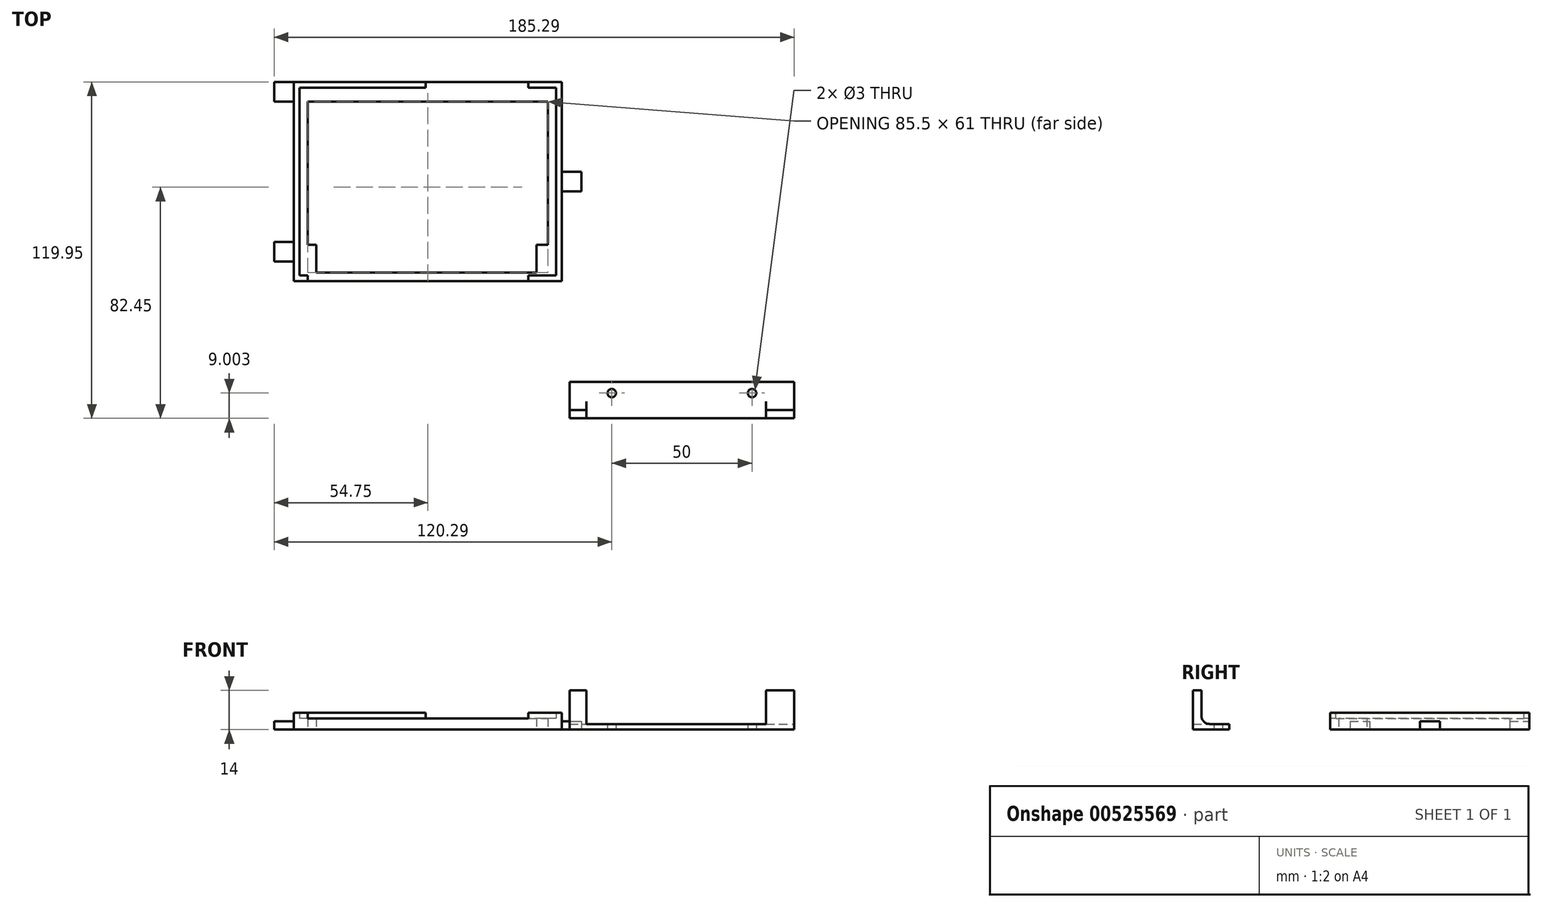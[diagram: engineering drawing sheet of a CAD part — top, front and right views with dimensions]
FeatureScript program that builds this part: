
annotation { "Feature Type Name" : "Feature", "Feature Type Description" : "" }
export const myFeature = defineFeature(function(context is Context, id is Id, definition is map)
    precondition{}
    {
        {
            var Q0;
            Q0=qCreatedBy(makeId("Top.planeOp"),FACE);
            var sketch = newSketch(context, id + "F0", { "sketchPlane" : qUnion([Q0])});
            skLineSegment(sketch, "E0.bottom", {"start": v(45.75, -33.5) * mm, "end": v(-45.75, -33.5) * mm});
            skLineSegment(sketch, "E0.top", {"start": v(45.75, 33.5) * mm, "end": v(-45.75, 33.5) * mm});
            skLineSegment(sketch, "E0.left", {"start": v(45.75, -33.5) * mm, "end": v(45.75, 33.5) * mm});
            skLineSegment(sketch, "E0.right", {"start": v(-45.75, -33.5) * mm, "end": v(-45.75, 33.5) * mm});
            skPoint(sketch, "E0.middle", {"position": v(0, 0) * mm});
            skLineSegment(sketch, "E1.bottom", {"start": v(47.75, -35.5) * mm, "end": v(-47.75, -35.5) * mm});
            skLineSegment(sketch, "E1.top", {"start": v(47.75, 35.5) * mm, "end": v(-47.75, 35.5) * mm});
            skLineSegment(sketch, "E1.left", {"start": v(47.75, -35.5) * mm, "end": v(47.75, 35.5) * mm});
            skLineSegment(sketch, "E1.right", {"start": v(-47.75, -35.5) * mm, "end": v(-47.75, 35.5) * mm});
            skSolve(sketch);
        }
        {
            var Q0;
            Q0=qSketchRegion(id+"F0",true);
            extrude(context, id + "F1", {"entities" : qUnion([Q0]), "depth" : 6 * mm, "offsetDistance" : 25 * mm});
        }
        {
            var Q0;
            Q0=makeQuery(id+"F1.opExtrude","CAP_FACE",FACE,{"disambiguationData":[OSD([sQuery(id+"F0.wireOp",EDGE,"E0.bottom"),sQuery(id+"F0.wireOp",EDGE,"E0.top"),sQuery(id+"F0.wireOp",EDGE,"E0.left"),sQuery(id+"F0.wireOp",EDGE,"E0.right"),sQuery(id+"F0.wireOp",EDGE,"E1.bottom"),sQuery(id+"F0.wireOp",EDGE,"E1.top"),sQuery(id+"F0.wireOp",EDGE,"E1.left"),sQuery(id+"F0.wireOp",EDGE,"E1.right")])],"isStart":true});
            var sketch = newSketch(context, id + "F2", { "sketchPlane" : qUnion([Q0])});
            skLineSegment(sketch, "E2.bottom", {"start": v(45.75, 33.5) * mm, "end": v(-45.75, 33.5) * mm});
            skLineSegment(sketch, "E2.top", {"start": v(45.75, -33.5) * mm, "end": v(-45.75, -33.5) * mm});
            skLineSegment(sketch, "E2.left", {"start": v(45.75, 33.5) * mm, "end": v(45.75, -33.5) * mm});
            skLineSegment(sketch, "E2.right", {"start": v(-45.75, 33.5) * mm, "end": v(-45.75, -33.5) * mm});
            skPoint(sketch, "E2.middle", {"position": v(0, 0) * mm});
            skLineSegment(sketch, "E3.bottom", {"start": v(-42.75, -28.5) * mm, "end": v(-30.75, -28.5) * mm});
            skLineSegment(sketch, "E3.top", {"start": v(-39.75, 32.5) * mm, "end": v(38.75, 32.5) * mm});
            skLineSegment(sketch, "E3.left", {"start": v(-42.75, -28.5) * mm, "end": v(-42.75, 22.5) * mm});
            skLineSegment(sketch, "E3.right", {"start": v(42.75, -28.5) * mm, "end": v(42.75, 22.5) * mm});
            skLineSegment(sketch, "E4", {"start": v(42.75, 22.5) * mm, "end": v(38.75, 22.5) * mm});
            skLineSegment(sketch, "E5", {"start": v(38.75, 22.5) * mm, "end": v(38.75, 32.5) * mm});
            skLineSegment(sketch, "E6", {"start": v(-30.75, -28.5) * mm, "end": v(-30.75, -28.5) * mm});
            skLineSegment(sketch, "E7", {"start": v(-30.75, -28.5) * mm, "end": v(-20.75, -28.5) * mm});
            skLineSegment(sketch, "E8", {"start": v(-20.75, -28.5) * mm, "end": v(-20.75, -28.5) * mm});
            skLineSegment(sketch, "E9.trimOffspring", {"start": v(-20.75, -28.5) * mm, "end": v(42.75, -28.5) * mm});
            skLineSegment(sketch, "E10", {"start": v(-42.75, 22.5) * mm, "end": v(-39.75, 22.5) * mm});
            skLineSegment(sketch, "E11", {"start": v(-39.75, 22.5) * mm, "end": v(-39.75, 32.5) * mm});
            skSolve(sketch);
        }
        {
            var Q0;
            Q0=qSketchRegion(id+"F2",true);
            extrude(context, id + "F3", {"entities" : qUnion([Q0]), "operationType" : NewBodyOperationType.ADD, "oppositeDirection" : true, "depth" : 4 * mm, "offsetDistance" : 25 * mm});
        }
        {
            var Q0;
            Q0=makeQuery(id+"F1.opExtrude","CAP_FACE",FACE,{"disambiguationData":[OSD([sQuery(id+"F0.wireOp",EDGE,"E0.bottom"),sQuery(id+"F0.wireOp",EDGE,"E0.top"),sQuery(id+"F0.wireOp",EDGE,"E0.left"),sQuery(id+"F0.wireOp",EDGE,"E0.right"),sQuery(id+"F0.wireOp",EDGE,"E1.bottom"),sQuery(id+"F0.wireOp",EDGE,"E1.top"),sQuery(id+"F0.wireOp",EDGE,"E1.left"),sQuery(id+"F0.wireOp",EDGE,"E1.right")])],"isStart":false});
            var sketch = newSketch(context, id + "F4", { "sketchPlane" : qUnion([Q0])});
            skLineSegment(sketch, "E12.bottom", {"start": v(-42.75, -33.5) * mm, "end": v(35.75, -33.5) * mm});
            skLineSegment(sketch, "E12.top", {"start": v(-42.75, -35.5) * mm, "end": v(35.75, -35.5) * mm});
            skLineSegment(sketch, "E12.left", {"start": v(-42.75, -33.5) * mm, "end": v(-42.75, -35.5) * mm});
            skLineSegment(sketch, "E12.right", {"start": v(35.75, -33.5) * mm, "end": v(35.75, -35.5) * mm});
            skLineSegment(sketch, "E13.bottom", {"start": v(-0.75, 35.5) * mm, "end": v(35.75, 35.5) * mm});
            skLineSegment(sketch, "E13.top", {"start": v(-0.75, 33.5) * mm, "end": v(35.75, 33.5) * mm});
            skLineSegment(sketch, "E13.left", {"start": v(-0.75, 35.5) * mm, "end": v(-0.75, 33.5) * mm});
            skLineSegment(sketch, "E13.right", {"start": v(35.75, 35.5) * mm, "end": v(35.75, 33.5) * mm});
            skSolve(sketch);
        }
        {
            var Q0;
            Q0=qSketchRegion(id+"F4",true);
            extrude(context, id + "F5", {"entities" : qUnion([Q0]), "operationType" : NewBodyOperationType.REMOVE, "oppositeDirection" : true, "depth" : 2 * mm, "offsetDistance" : 25 * mm});
        }
        {
            var Q0;
            Q0=makeQuery(id+"F3.boolean.opBoolean","MERGE",FACE,{"derivedFrom":[makeQuery(id+"F1.opExtrude","CAP_FACE",FACE,{"disambiguationData":[OSD([sQuery(id+"F0.wireOp",EDGE,"E0.bottom"),sQuery(id+"F0.wireOp",EDGE,"E0.top"),sQuery(id+"F0.wireOp",EDGE,"E0.left"),sQuery(id+"F0.wireOp",EDGE,"E0.right"),sQuery(id+"F0.wireOp",EDGE,"E1.bottom"),sQuery(id+"F0.wireOp",EDGE,"E1.top"),sQuery(id+"F0.wireOp",EDGE,"E1.left"),sQuery(id+"F0.wireOp",EDGE,"E1.right")])],"isStart":true}),makeQuery(id+"F3.opExtrude","CAP_FACE",FACE,{"disambiguationData":[OSD([sQuery(id+"F2.wireOp",EDGE,"E2.bottom"),sQuery(id+"F2.wireOp",EDGE,"E2.top"),sQuery(id+"F2.wireOp",EDGE,"E2.left"),sQuery(id+"F2.wireOp",EDGE,"E2.right"),sQuery(id+"F2.wireOp",EDGE,"E3.bottom"),sQuery(id+"F2.wireOp",EDGE,"E3.top"),sQuery(id+"F2.wireOp",EDGE,"E3.left"),sQuery(id+"F2.wireOp",EDGE,"E3.right"),sQuery(id+"F2.wireOp",EDGE,"E4"),sQuery(id+"F2.wireOp",EDGE,"E5"),sQuery(id+"F2.wireOp",EDGE,"E6"),sQuery(id+"F2.wireOp",EDGE,"E7"),sQuery(id+"F2.wireOp",EDGE,"E8"),sQuery(id+"F2.wireOp",EDGE,"E9.trimOffspring")])],"isStart":true})]});
            var sketch = newSketch(context, id + "F6", { "sketchPlane" : qUnion([Q0])});
            skLineSegment(sketch, "E14.bottom", {"start": v(-47.75, 21.5) * mm, "end": v(-54.75, 21.5) * mm});
            skLineSegment(sketch, "E14.top", {"start": v(-47.75, 28.5) * mm, "end": v(-54.75, 28.5) * mm});
            skLineSegment(sketch, "E14.left", {"start": v(-47.75, 21.5) * mm, "end": v(-47.75, 28.5) * mm});
            skLineSegment(sketch, "E14.right", {"start": v(-54.75, 21.5) * mm, "end": v(-54.75, 28.5) * mm});
            skLineSegment(sketch, "E15.bottom", {"start": v(-47.75, -35.5) * mm, "end": v(-54.75, -35.5) * mm});
            skLineSegment(sketch, "E15.top", {"start": v(-47.75, -28.5) * mm, "end": v(-54.75, -28.5) * mm});
            skLineSegment(sketch, "E15.left", {"start": v(-47.75, -35.5) * mm, "end": v(-47.75, -28.5) * mm});
            skLineSegment(sketch, "E15.right", {"start": v(-54.75, -35.5) * mm, "end": v(-54.75, -28.5) * mm});
            skPoint(sketch, "E16", {"position": v(-51.25, -32) * mm});
            skPoint(sketch, "E16.positionSnap0", {"position": v(-51.25, -35.5) * mm});
            skPoint(sketch, "E16.positionSnap1", {"position": v(-54.75, -32) * mm});
            skPoint(sketch, "E17", {"position": v(-51.25, 25) * mm});
            skPoint(sketch, "E17.positionSnap0", {"position": v(-51.25, 21.5) * mm});
            skPoint(sketch, "E17.positionSnap1", {"position": v(-54.75, 25) * mm});
            skLineSegment(sketch, "E18.bottom", {"start": v(47.75, -3.5) * mm, "end": v(54.75, -3.5) * mm});
            skLineSegment(sketch, "E18.top", {"start": v(47.75, 3.5) * mm, "end": v(54.75, 3.5) * mm});
            skLineSegment(sketch, "E18.left", {"start": v(47.75, -3.5) * mm, "end": v(47.75, 3.5) * mm});
            skLineSegment(sketch, "E18.right", {"start": v(54.75, -3.5) * mm, "end": v(54.75, 3.5) * mm});
            skPoint(sketch, "E19", {"position": v(51.25, 0) * mm});
            skPoint(sketch, "E19.positionSnap0", {"position": v(54.75, 0) * mm});
            skPoint(sketch, "E19.positionSnap1", {"position": v(51.25, 3.5) * mm});
            skSolve(sketch);
        }
        {
            var Q0;
            Q0=qSketchRegion(id+"F6",true);
            extrude(context, id + "F7", {"entities" : qUnion([Q0]), "operationType" : NewBodyOperationType.ADD, "oppositeDirection" : true, "depth" : 3 * mm, "offsetDistance" : 25 * mm});
        }
        {
            var Q0;
            Q0=qCreatedBy(makeId("Top.planeOp"),FACE);
            var sketch = newSketch(context, id + "F8", { "sketchPlane" : qUnion([Q0])});
            skLineSegment(sketch, "E20.bottom", {"start": v(130.54, -84.45) * mm, "end": v(50.54, -84.45) * mm});
            skLineSegment(sketch, "E20.top", {"start": v(130.54, -71.45) * mm, "end": v(50.54, -71.45) * mm});
            skLineSegment(sketch, "E20.left", {"start": v(130.54, -84.45) * mm, "end": v(130.54, -71.45) * mm});
            skLineSegment(sketch, "E20.right", {"start": v(50.54, -84.45) * mm, "end": v(50.54, -71.45) * mm});
            skPoint(sketch, "E20.middle", {"position": v(90.54, -77.95) * mm});
            skCircle(sketch, "E21", {"center": v(65.54, -75.45) * mm, "radius": 1.5 * mm});
            skCircle(sketch, "E22", {"center": v(115.54, -75.45) * mm, "radius": 1.5 * mm});
            skSolve(sketch);
        }
        {
            var Q0;
            Q0=qSketchRegion(id+"F8",true);
            extrude(context, id + "F9", {"entities" : qUnion([Q0]), "depth" : 2 * mm, "offsetDistance" : 25 * mm});
        }
        {
            var Q0;
            Q0=makeQuery(id+"F9.opExtrude","SWEPT_FACE",FACE,{"disambiguationData":[OSD([sQuery(id+"F8.wireOp",EDGE,"E20.bottom")])]});
            var sketch = newSketch(context, id + "F10", { "sketchPlane" : qUnion([Q0])});
            skLineSegment(sketch, "E23.bottom", {"start": v(120.54, 0) * mm, "end": v(130.54, 0) * mm});
            skLineSegment(sketch, "E23.top", {"start": v(120.54, 14) * mm, "end": v(130.54, 14) * mm});
            skLineSegment(sketch, "E23.left", {"start": v(130.54, 0) * mm, "end": v(130.54, 14) * mm});
            skLineSegment(sketch, "E23.right", {"start": v(120.54, 0) * mm, "end": v(120.54, 14) * mm});
            skLineSegment(sketch, "E24.bottom", {"start": v(50.54, 0) * mm, "end": v(56.54, 0) * mm});
            skLineSegment(sketch, "E24.top", {"start": v(50.54, 14) * mm, "end": v(56.54, 14) * mm});
            skLineSegment(sketch, "E24.left", {"start": v(50.54, 0) * mm, "end": v(50.54, 14) * mm});
            skLineSegment(sketch, "E24.right", {"start": v(56.54, 0) * mm, "end": v(56.54, 14) * mm});
            skSolve(sketch);
        }
        {
            var Q0;
            Q0=qSketchRegion(id+"F10",true);
            extrude(context, id + "F11", {"entities" : qUnion([Q0]), "operationType" : NewBodyOperationType.ADD, "oppositeDirection" : true, "depth" : 3 * mm, "offsetDistance" : 25 * mm});
        }
        {
            var Q0;
            Q0=makeQuery(id+"F11.boolean.opBoolean","INTERSECT",EDGE,{"derivedFrom":[makeQuery(id+"F9.opExtrude","CAP_FACE",FACE,{"disambiguationData":[OSD([sQuery(id+"F8.wireOp",EDGE,"E20.bottom"),sQuery(id+"F8.wireOp",EDGE,"E20.top"),sQuery(id+"F8.wireOp",EDGE,"E20.left"),sQuery(id+"F8.wireOp",EDGE,"E20.right"),sQuery(id+"F8.wireOp",EDGE,"E21"),sQuery(id+"F8.wireOp",EDGE,"E22")])],"isStart":false}),makeQuery(id+"F11.opExtrude","CAP_FACE",FACE,{"disambiguationData":[OSD([sQuery(id+"F10.wireOp",EDGE,"E24.bottom"),sQuery(id+"F10.wireOp",EDGE,"E24.top"),sQuery(id+"F10.wireOp",EDGE,"E24.left"),sQuery(id+"F10.wireOp",EDGE,"E24.right")])],"isStart":false})]});
            var Q1;
            Q1=makeQuery(id+"F11.boolean.opBoolean","INTERSECT",EDGE,{"derivedFrom":[makeQuery(id+"F9.opExtrude","CAP_FACE",FACE,{"disambiguationData":[OSD([sQuery(id+"F8.wireOp",EDGE,"E20.bottom"),sQuery(id+"F8.wireOp",EDGE,"E20.top"),sQuery(id+"F8.wireOp",EDGE,"E20.left"),sQuery(id+"F8.wireOp",EDGE,"E20.right"),sQuery(id+"F8.wireOp",EDGE,"E21"),sQuery(id+"F8.wireOp",EDGE,"E22")])],"isStart":false}),makeQuery(id+"F11.opExtrude","CAP_FACE",FACE,{"disambiguationData":[OSD([sQuery(id+"F10.wireOp",EDGE,"E23.bottom"),sQuery(id+"F10.wireOp",EDGE,"E23.top"),sQuery(id+"F10.wireOp",EDGE,"E23.left"),sQuery(id+"F10.wireOp",EDGE,"E23.right")])],"isStart":false})]});
            fillet(context, id + "F12", {"entities" : qUnion([Q0, Q1]), "radius" : 3 * mm, "tangentPropagation" : true, "allowEdgeOverflow" : false});
        }
    });
